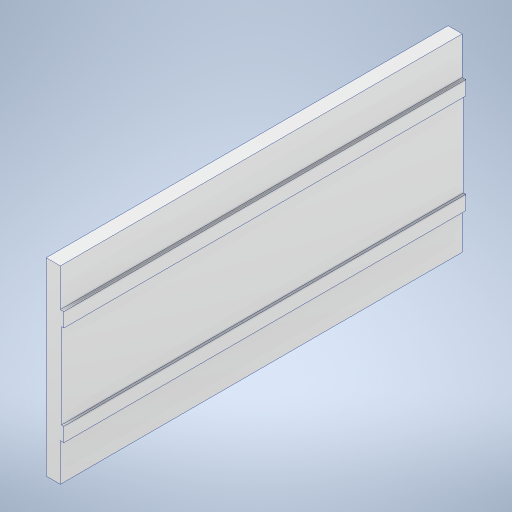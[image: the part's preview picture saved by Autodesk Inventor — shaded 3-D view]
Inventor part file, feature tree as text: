
AUTODESK INVENTOR PART (.ipt)
format: ipt  version: 2024 (Build 280153000, 153)  size: 347,136 bytes
history: native  units: mm
features: extrude x7, sketch x7, projected_geometry x3
ambient origin geometry x8: Origin, YZ Plane, XZ Plane, XY Plane, X Axis, Y Axis, Z Axis, Center Point
bodies: Solid1 (feature_tree)
feature tree (17):
  extrude  "Extrusion1"  Depth=160.0mm TaperAngle=0.0deg
  extrude  "Extrusion2"  Depth=25.0mm
  extrude  "Extrusion3"  Depth=45.0mm
  extrude  "Extrusion4"  Depth=4.0mm
  extrude  "Extrusion5"  Depth=80.0mm
  extrude  "Extrusion6"  Depth=150.0mm TaperAngle=0.0deg
  extrude  "Extrusion7"  Depth=340.0mm
  sketch  "Sketch1"  dims[d0=475.0mm d1=160.0mm d2=0.0mm]
  sketch  "Sketch2"  dims[d4=25.0mm d5=25.0mm]
  sketch  "Sketch3"  dims[d6=10.0mm d7=45.0mm]
  sketch  "Sketch4"  dims[d8=45.0mm d9=4.0mm]
  projected_geometry  "Projected Loop1"
  projected_geometry  "Projected Loop2"
  sketch  "Sketch5"  dims[d10=36.0mm d11=80.0mm]
  projected_geometry  "Projected Loop3"
  sketch  "Sketch6"  dims[d12=80.0mm d13=150.0mm d14=0.0mm]
  sketch  "Sketch7"  dims[d15=20.0mm d16=340.0mm d17=200.0mm d18=0.0mm d19=30.0mm d20=0.0mm d21=5.0mm d22=0.0mm d23=13.0mm d24=13.0mm d25=3.0mm d26=500.0mm d27=0.0mm d28=1.0mm d29=1.0mm d30=2.0mm d31=1000.0mm d32=0.0mm]
